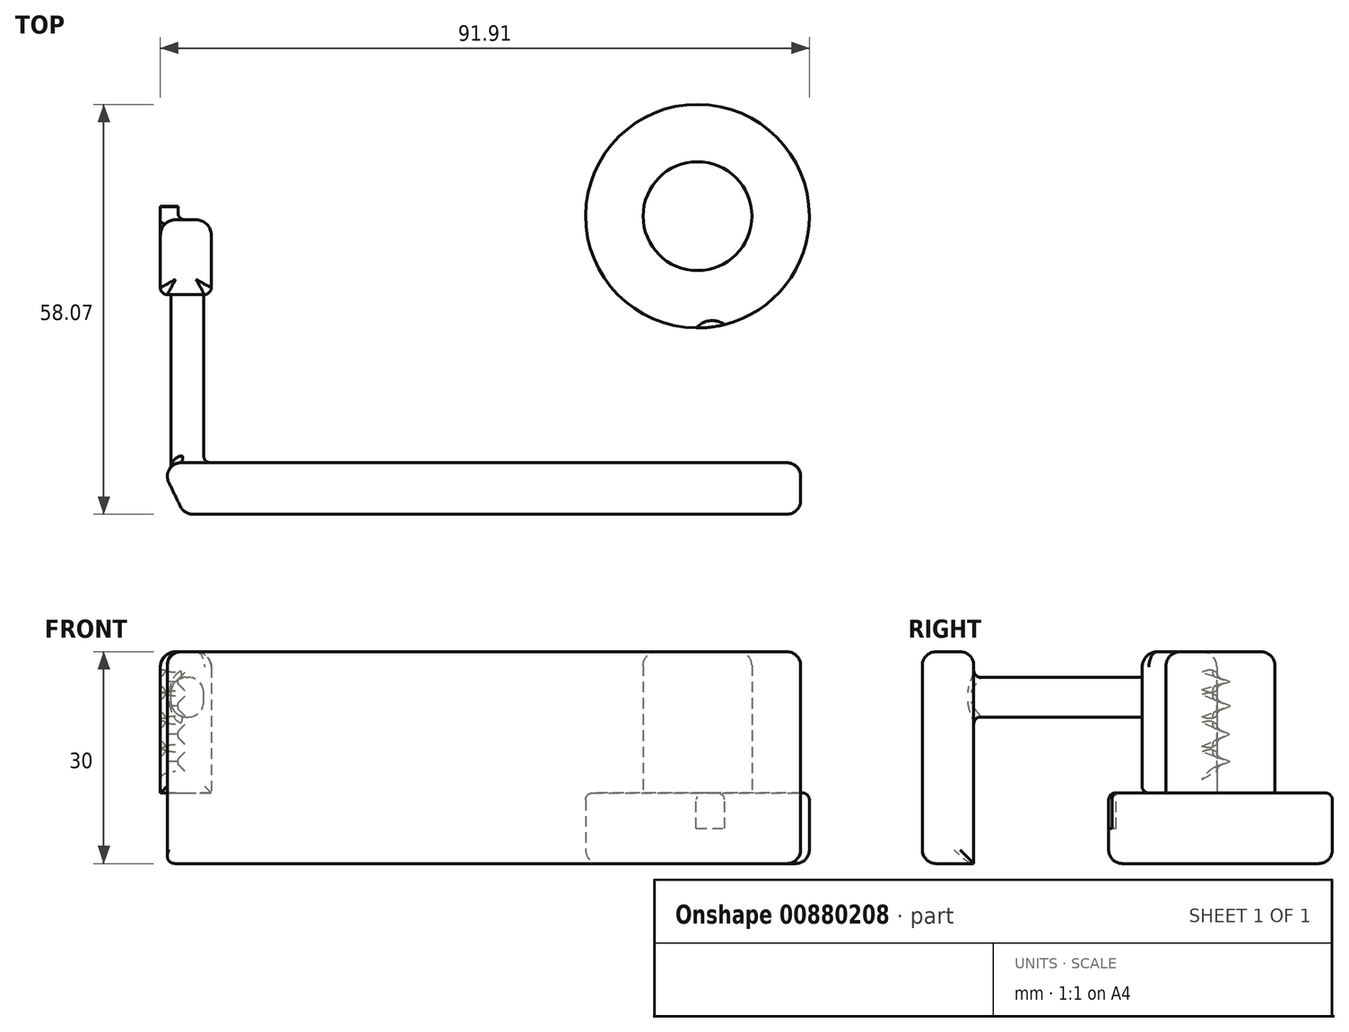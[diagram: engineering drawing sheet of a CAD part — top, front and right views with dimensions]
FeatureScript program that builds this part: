
annotation { "Feature Type Name" : "Feature", "Feature Type Description" : "" }
export const myFeature = defineFeature(function(context is Context, id is Id, definition is map)
    precondition{}
    {
        {
            var Q0;
            Q0=qCreatedBy(makeId("Top.planeOp"),FACE);
            var sketch = newSketch(context, id + "F0", { "sketchPlane" : qUnion([Q0])});
            skLineSegment(sketch, "E0", {"start": v(63.05, -17.14) * mm, "end": v(63.05, 11.68) * mm});
            skCircle(sketch, "E1", {"center": v(48.44, 17.8) * mm, "radius": 15.84 * mm});
            skFitSpline(sketch, "E2", {"points": [v(35.46, 26.9) * mm, v(16.93, 8.4) * mm, v(-6.27, 10.49) * mm, v(-19.03, 21.44) * mm, v(-36, 19.85) * mm, v(-24.25, -24.43) * mm], "startDerivative": vector(-84.65, -85.57) * mm, "endDerivative": vector(94.53, -192.44) * mm});
            skLineSegment(sketch, "E3", {"start": v(-27.75, -17.14) * mm, "end": v(63.05, -17.14) * mm});
            skLineSegment(sketch, "E4", {"start": v(-24.25, -24.43) * mm, "end": v(63.05, -24.43) * mm});
            skLineSegment(sketch, "E5", {"start": v(63.05, -24.43) * mm, "end": v(63.05, -17.14) * mm});
            skSolve(sketch);
        }
        {
            var Q0;
            {var subQ0=sQuery(id+"F0.wireOp",EDGE,"E1");var subQ1=makeQuery(id+"F0.imprint","INTERSECT",VERTEX,{"derivedFrom":[sQuery(id+"F0.wireOp",EDGE,"E0"),subQ0]});Q0=makeQuery(id+"F0.imprint","IMPRINT",FACE,{"disambiguationData":[TD([[makeQuery(id+"F0.imprint","IMPRINT",EDGE,{"disambiguationData":[TD([[subQ1,1.0]])],"derivedFrom":subQ0}),1.0]])]});}
            var Q1;
            {var subQ0=sQuery(id+"F0.wireOp",EDGE,"E0");Q1=makeQuery(id+"F0.imprint","IMPRINT",FACE,{"disambiguationData":[TD([[makeQuery(id+"F0.imprint","IMPRINT",EDGE,{"derivedFrom":subQ0}),1.0]])]});}
            extrude(context, id + "F1", {"entities" : qUnion([Q0, Q1]), "depth" : 10 * mm, "offsetDistance" : 25.4 * mm});
        }
        {
            var Q0;
            {var subQ2=sQuery(id+"F0.wireOp",EDGE,"E3");Q0=makeQuery(id+"F0.imprint","IMPRINT",FACE,{"disambiguationData":[TD([[makeQuery(id+"F0.imprint","IMPRINT",EDGE,{"derivedFrom":subQ2}),-1.0]])]});}
            extrude(context, id + "F2", {"entities" : qUnion([Q0]), "operationType" : NewBodyOperationType.ADD, "depth" : 30 * mm, "offsetDistance" : 25 * mm});
        }
        {
            var Q0;
            Q0=makeQuery(id+"F1.opExtrude","CAP_FACE",FACE,{"disambiguationData":[OSD([sQuery(id+"F0.wireOp",EDGE,"E0"),sQuery(id+"F0.wireOp",EDGE,"E1"),sQuery(id+"F0.wireOp",EDGE,"E2"),sQuery(id+"F0.wireOp",EDGE,"E3")])],"isStart":false});
            var sketch = newSketch(context, id + "F3", { "sketchPlane" : qUnion([Q0])});
            skCircle(sketch, "E6", {"center": v(48.44, 17.8) * mm, "radius": 7.7 * mm});
            skLineSegment(sketch, "E7.bottom", {"start": v(-27.63, 17.29) * mm, "end": v(-20.42, 17.29) * mm});
            skLineSegment(sketch, "E7.top", {"start": v(-27.63, 6.69) * mm, "end": v(-20.42, 6.69) * mm});
            skLineSegment(sketch, "E7.left", {"start": v(-27.63, 17.29) * mm, "end": v(-27.63, 6.69) * mm});
            skLineSegment(sketch, "E7.right", {"start": v(-20.42, 17.29) * mm, "end": v(-20.42, 6.69) * mm});
            skPoint(sketch, "E8", {"position": v(-8.96, 0) * mm});
            skPoint(sketch, "E9", {"position": v(20.74, 0) * mm});
            skPoint(sketch, "E10", {"position": v(50.52, 0) * mm});
            skSolve(sketch);
        }
        {
            var Q0;
            Q0=makeQuery(id+"F3.imprint","IMPRINT",FACE,{"disambiguationData":[TD([[makeQuery(id+"F3.imprint","IMPRINT",EDGE,{"derivedFrom":sQuery(id+"F3.wireOp",EDGE,"E6")}),1.0]])]});
            var Q1;
            Q1=makeQuery(id+"F3.imprint","IMPRINT",FACE,{"disambiguationData":[TD([[makeQuery(id+"F3.imprint","IMPRINT",EDGE,{"derivedFrom":sQuery(id+"F3.wireOp",EDGE,"E7.bottom")}),-1.0]])]});
            extrude(context, id + "F4", {"entities" : qUnion([Q0, Q1]), "operationType" : NewBodyOperationType.ADD, "depth" : 20 * mm, "offsetDistance" : 25 * mm});
        }
        {
            var Q0;
            Q0=makeQuery(id+"F4.opExtrude","SWEPT_FACE",FACE,{"disambiguationData":[OSD([sQuery(id+"F3.wireOp",EDGE,"E7.left")])]});
            var sketch = newSketch(context, id + "F5", { "sketchPlane" : qUnion([Q0])});
            skLineSegment(sketch, "E11", {"start": v(-17.29, 13.76) * mm, "end": v(-19.15, 14.47) * mm});
            skLineSegment(sketch, "E12", {"start": v(-19.15, 14.47) * mm, "end": v(-14.05, 16.16) * mm});
            skLineSegment(sketch, "E13", {"start": v(-14.05, 16.16) * mm, "end": v(-19.09, 18.3) * mm});
            skLineSegment(sketch, "E14", {"start": v(-19.09, 18.3) * mm, "end": v(-14.05, 20.42) * mm});
            skLineSegment(sketch, "E15", {"start": v(-14.05, 20.42) * mm, "end": v(-19.2, 22.3) * mm});
            skLineSegment(sketch, "E16", {"start": v(-19.2, 22.3) * mm, "end": v(-14.05, 24.37) * mm});
            skLineSegment(sketch, "E17.bottom", {"start": v(-17.29, 10) * mm, "end": v(-6.69, 10) * mm});
            skLineSegment(sketch, "E17.top", {"start": v(-17.29, 30) * mm, "end": v(-6.69, 30) * mm});
            skLineSegment(sketch, "E17.left", {"start": v(-17.29, 10) * mm, "end": v(-17.29, 30) * mm});
            skLineSegment(sketch, "E17.right", {"start": v(-6.69, 10) * mm, "end": v(-6.69, 30) * mm});
            skLineSegment(sketch, "E18", {"start": v(-14.05, 24.37) * mm, "end": v(-19.15, 25.75) * mm});
            skLineSegment(sketch, "E19", {"start": v(-19.15, 25.75) * mm, "end": v(-17.29, 26.37) * mm});
            skSolve(sketch);
        }
        {
            var Q0;
            Q0 = qSketchRegion(id + "F5", true);
            extrude(context, id + "F6", {"entities" : qUnion([Q0]), "operationType" : NewBodyOperationType.ADD, "oppositeDirection" : true, "depth" : 2.5 * mm, "offsetDistance" : 25 * mm});
        }
        {
            var Q0;
            Q0=makeQuery(id+"F4.opExtrude","SWEPT_FACE",FACE,{"disambiguationData":[OSD([sQuery(id+"F3.wireOp",EDGE,"E7.top")])]});
            var sketch = newSketch(context, id + "F7", { "sketchPlane" : qUnion([Q0])});
            skLineSegment(sketch, "E20.bottom", {"start": v(-26.13, 20.76) * mm, "end": v(-21.5, 20.76) * mm});
            skLineSegment(sketch, "E20.top", {"start": v(-26.13, 26.39) * mm, "end": v(-21.5, 26.39) * mm});
            skLineSegment(sketch, "E20.left", {"start": v(-26.13, 20.76) * mm, "end": v(-26.13, 26.39) * mm});
            skLineSegment(sketch, "E20.right", {"start": v(-21.5, 20.76) * mm, "end": v(-21.5, 26.39) * mm});
            skSolve(sketch);
        }
        {
            var Q0;
            Q0 = qSketchRegion(id + "F7", true);
            extrude(context, id + "F8", {"entities" : qUnion([Q0]), "operationType" : NewBodyOperationType.ADD, "depth" : 25 * mm, "offsetDistance" : 25 * mm});
        }
        {
            var Q0;
            Q0=sQuery(id+"F3.wireOp",VERTEX,"E8");
            var Q1;
            Q1=sQuery(id+"F3.wireOp",VERTEX,"E9");
            var Q2;
            Q2=sQuery(id+"F3.wireOp",VERTEX,"E10");
            var Q3;
            Q3=makeQuery(id+"F1.opExtrude","SWEPT_BODY",BODY,{"disambiguationData":[OSD([sQuery(id+"F0.wireOp",EDGE,"E0"),sQuery(id+"F0.wireOp",EDGE,"E1"),sQuery(id+"F0.wireOp",EDGE,"E2"),sQuery(id+"F0.wireOp",EDGE,"E3")])]});
            hole(context, id + "F9", {"style" : HoleStyle.C_BORE, "endStyle" : HoleEndStyle.THROUGH, "holeDiameter" : 4 * mm, "cBoreDiameter" : 6 * mm, "cBoreDepth" : 5 * mm, "majorDiameter" : 5 * mm, "isTappedThrough" : true, "tappedDepth" : 12 * mm, "tapClearance" : 3, "locations" : qUnion([Q0, Q1, Q2]), "scope" : qUnion([Q3])});
        }
        {
            var Q0;
            Q0=makeQuery(id+"F2.opExtrude","SWEPT_EDGE",EDGE,{"disambiguationData":[OSD([sQuery(id+"F0.wireOp",EDGE,"E2"),sQuery(id+"F0.wireOp",EDGE,"E4")])]});
            var Q1;
            Q1=makeQuery(id+"F2.opExtrude","CAP_EDGE",EDGE,{"disambiguationData":[OSD([sQuery(id+"F0.wireOp",EDGE,"E4")])],"isStart":false});
            var Q2;
            Q2=makeQuery(id+"F2.opExtrude","SWEPT_EDGE",EDGE,{"disambiguationData":[OSD([sQuery(id+"F0.wireOp",EDGE,"E4"),sQuery(id+"F0.wireOp",EDGE,"E5")])]});
            var Q3;
            Q3=makeQuery(id+"F2.opExtrude","CAP_EDGE",EDGE,{"disambiguationData":[OSD([sQuery(id+"F0.wireOp",EDGE,"E4")])],"isStart":true});
            var Q4;
            {var subQ0=sQuery(id+"F0.wireOp",EDGE,"E2");Q4=makeQuery(id+"F2.boolean.opBoolean","MERGE",EDGE,{"derivedFrom":[makeQuery(id+"F1.opExtrude","CAP_EDGE",EDGE,{"disambiguationData":[OSD([subQ0])],"isStart":true}),makeQuery(id+"F2.opExtrude","CAP_EDGE",EDGE,{"disambiguationData":[OSD([subQ0])],"isStart":true})]});}
            var Q5;
            Q5=makeQuery(id+"F1.opExtrude","CAP_EDGE",EDGE,{"disambiguationData":[OSD([sQuery(id+"F0.wireOp",EDGE,"E1")])],"isStart":true});
            var Q6;
            Q6=makeQuery(id+"F2.boolean.opBoolean","MERGE",EDGE,{"derivedFrom":[makeQuery(id+"F1.opExtrude","CAP_EDGE",EDGE,{"disambiguationData":[OSD([sQuery(id+"F0.wireOp",EDGE,"E0")])],"isStart":true}),makeQuery(id+"F2.opExtrude","CAP_EDGE",EDGE,{"disambiguationData":[OSD([sQuery(id+"F0.wireOp",EDGE,"E5")])],"isStart":true})]});
            var Q7;
            Q7=makeQuery(id+"F1.opExtrude","CAP_EDGE",EDGE,{"disambiguationData":[OSD([sQuery(id+"F0.wireOp",EDGE,"E2")])],"isStart":false});
            var Q8;
            Q8=makeQuery(id+"F2.opExtrude","SWEPT_EDGE",EDGE,{"disambiguationData":[OSD([sQuery(id+"F0.wireOp",EDGE,"E0"),sQuery(id+"F0.wireOp",EDGE,"E3"),sQuery(id+"F0.wireOp",EDGE,"E5")])]});
            var Q9;
            Q9=makeQuery(id+"F2.opExtrude","CAP_EDGE",EDGE,{"disambiguationData":[OSD([sQuery(id+"F0.wireOp",EDGE,"E5")])],"isStart":false});
            var Q10;
            Q10=makeQuery(id+"F2.opExtrude","CAP_EDGE",EDGE,{"disambiguationData":[OSD([sQuery(id+"F0.wireOp",EDGE,"E3")])],"isStart":false});
            var Q11;
            Q11=makeQuery(id+"F2.opExtrude","SWEPT_EDGE",EDGE,{"disambiguationData":[OSD([sQuery(id+"F0.wireOp",EDGE,"E2"),sQuery(id+"F0.wireOp",EDGE,"E3")])]});
            var Q12;
            Q12=makeQuery(id+"F2.opExtrude","CAP_EDGE",EDGE,{"disambiguationData":[OSD([sQuery(id+"F0.wireOp",EDGE,"E2")])],"isStart":false});
            var Q13;
            Q13=makeQuery(id+"F4.opExtrude","CAP_EDGE",EDGE,{"disambiguationData":[OSD([sQuery(id+"F3.wireOp",EDGE,"E6")])],"isStart":false});
            var Q14;
            Q14=makeQuery(id+"F1.opExtrude","CAP_EDGE",EDGE,{"disambiguationData":[OSD([sQuery(id+"F0.wireOp",EDGE,"E3")])],"isStart":false});
            fillet(context, id + "F10", {"entities" : qUnion([Q0, Q1, Q2, Q3, Q4, Q5, Q6, Q7, Q8, Q9, Q10, Q11, Q12, Q13, Q14]), "radius" : 1.93 * mm, "tangentPropagation" : true, "allowEdgeOverflow" : false});
        }
        {
            var Q0;
            Q0=makeQuery(id+"F1.opExtrude","CAP_EDGE",EDGE,{"disambiguationData":[OSD([sQuery(id+"F0.wireOp",EDGE,"E0")])],"isStart":false});
            var Q1;
            Q1=makeQuery(id+"F8.opExtrude","SWEPT_EDGE",EDGE,{"disambiguationData":[OSD([sQuery(id+"F7.wireOp",EDGE,"E20.top"),sQuery(id+"F7.wireOp",EDGE,"E20.left")])]});
            var Q2;
            Q2=makeQuery(id+"F8.opExtrude","SWEPT_EDGE",EDGE,{"disambiguationData":[OSD([sQuery(id+"F7.wireOp",EDGE,"E20.bottom"),sQuery(id+"F7.wireOp",EDGE,"E20.left")])]});
            var Q3;
            Q3=makeQuery(id+"F8.opExtrude","SWEPT_EDGE",EDGE,{"disambiguationData":[OSD([sQuery(id+"F7.wireOp",EDGE,"E20.top"),sQuery(id+"F7.wireOp",EDGE,"E20.right")])]});
            var Q4;
            Q4=makeQuery(id+"F8.opExtrude","SWEPT_EDGE",EDGE,{"disambiguationData":[OSD([sQuery(id+"F7.wireOp",EDGE,"E20.bottom"),sQuery(id+"F7.wireOp",EDGE,"E20.right")])]});
            var Q5;
            Q5=makeQuery(id+"F4.opExtrude","CAP_EDGE",EDGE,{"disambiguationData":[OSD([sQuery(id+"F3.wireOp",EDGE,"E7.top")])],"isStart":false});
            var Q6;
            Q6=makeQuery(id+"F4.opExtrude","CAP_EDGE",EDGE,{"disambiguationData":[OSD([sQuery(id+"F3.wireOp",EDGE,"E7.left")])],"isStart":false});
            var Q7;
            Q7=makeQuery(id+"F4.opExtrude","CAP_EDGE",EDGE,{"disambiguationData":[OSD([sQuery(id+"F3.wireOp",EDGE,"E7.right")])],"isStart":false});
            var Q8;
            Q8=makeQuery(id+"F4.opExtrude","CAP_EDGE",EDGE,{"disambiguationData":[OSD([sQuery(id+"F3.wireOp",EDGE,"E7.bottom")])],"isStart":false});
            var Q9;
            Q9=makeQuery(id+"F4.opExtrude","SWEPT_EDGE",EDGE,{"disambiguationData":[OSD([sQuery(id+"F3.wireOp",EDGE,"E7.bottom"),sQuery(id+"F3.wireOp",EDGE,"E7.right")])]});
            var Q10;
            {var subQ0=sQuery(id+"F5.wireOp",EDGE,"E14");var subQ2=sQuery(id+"F3.wireOp",EDGE,"E7.left");var subQ3=sQuery(id+"F3.wireOp",EDGE,"E7.bottom");Q10=makeQuery(id+"F6.boolean.opBoolean","SPLIT",EDGE,{"disambiguationData":[TD([makeQuery(id+"F6.opExtrude","SWEPT_FACE",FACE,{"disambiguationData":[OSD([subQ0])]})])],"derivedFrom":makeQuery(id+"F4.opExtrude","SWEPT_EDGE",EDGE,{"disambiguationData":[OSD([subQ3,subQ2])]})});}
            var Q11;
            {var subQ0=sQuery(id+"F5.wireOp",EDGE,"E16");var subQ2=sQuery(id+"F3.wireOp",EDGE,"E7.left");var subQ3=sQuery(id+"F3.wireOp",EDGE,"E7.bottom");Q11=makeQuery(id+"F6.boolean.opBoolean","SPLIT",EDGE,{"disambiguationData":[TD([makeQuery(id+"F6.opExtrude","SWEPT_FACE",FACE,{"disambiguationData":[OSD([subQ0])]})])],"derivedFrom":makeQuery(id+"F4.opExtrude","SWEPT_EDGE",EDGE,{"disambiguationData":[OSD([subQ3,subQ2])]})});}
            var Q12;
            {var subQ0=sQuery(id+"F3.wireOp",EDGE,"E7.left");var subQ1=sQuery(id+"F5.wireOp",EDGE,"E19");var subQ2=sQuery(id+"F3.wireOp",EDGE,"E7.bottom");Q12=makeQuery(id+"F6.boolean.opBoolean","SPLIT",EDGE,{"disambiguationData":[TD([makeQuery(id+"F6.opExtrude","SWEPT_FACE",FACE,{"disambiguationData":[OSD([subQ1])]})])],"derivedFrom":makeQuery(id+"F4.opExtrude","SWEPT_EDGE",EDGE,{"disambiguationData":[OSD([subQ2,subQ0])]})});}
            var Q13;
            {var subQ0=sQuery(id+"F5.wireOp",EDGE,"E11");var subQ1=sQuery(id+"F3.wireOp",EDGE,"E7.bottom");var subQ2=sQuery(id+"F3.wireOp",EDGE,"E7.left");Q13=makeQuery(id+"F6.boolean.opBoolean","SPLIT",EDGE,{"disambiguationData":[TD([makeQuery(id+"F6.opExtrude","SWEPT_FACE",FACE,{"disambiguationData":[OSD([subQ0])]})])],"derivedFrom":makeQuery(id+"F4.opExtrude","SWEPT_EDGE",EDGE,{"disambiguationData":[OSD([subQ1,subQ2])]})});}
            var Q14;
            {var subQ1=sQuery(id+"F5.wireOp",EDGE,"E12");var subQ2=sQuery(id+"F3.wireOp",EDGE,"E7.left");var subQ3=sQuery(id+"F3.wireOp",EDGE,"E7.bottom");Q14=makeQuery(id+"F6.boolean.opBoolean","SPLIT",EDGE,{"disambiguationData":[TD([makeQuery(id+"F6.opExtrude","SWEPT_FACE",FACE,{"disambiguationData":[OSD([subQ1])]})])],"derivedFrom":makeQuery(id+"F4.opExtrude","SWEPT_EDGE",EDGE,{"disambiguationData":[OSD([subQ3,subQ2])]})});}
            fillet(context, id + "F11", {"entities" : qUnion([Q0, Q1, Q2, Q3, Q4, Q5, Q6, Q7, Q8, Q9, Q10, Q11, Q12, Q13, Q14]), "radius" : 2.17 * mm, "tangentPropagation" : true, "allowEdgeOverflow" : false});
        }
        {
            var Q0;
            Q0=makeQuery(id+"F9.hole-2.boolean.opBoolean","COPY",EDGE,{"derivedFrom":makeQuery(id+"F9.hole-2.opRevolve","SWEPT_EDGE",EDGE,{"disambiguationData":[OSD([sQuery(id+"F9.hole-2.sketch.wireOp",EDGE,"cbore_start_line_2"),sQuery(id+"F9.hole-2.sketch.wireOp",EDGE,"cbore_start_line_3")])]})});
            var Q1;
            Q1=makeQuery(id+"F9.hole-1.boolean.opBoolean","COPY",EDGE,{"derivedFrom":makeQuery(id+"F9.hole-1.opRevolve","SWEPT_EDGE",EDGE,{"disambiguationData":[OSD([sQuery(id+"F9.hole-1.sketch.wireOp",EDGE,"cbore_start_line_2"),sQuery(id+"F9.hole-1.sketch.wireOp",EDGE,"cbore_start_line_3")])]})});
            var Q2;
            Q2=makeQuery(id+"F9.hole-0.boolean.opBoolean","COPY",EDGE,{"derivedFrom":makeQuery(id+"F9.hole-0.opRevolve","SWEPT_EDGE",EDGE,{"disambiguationData":[OSD([sQuery(id+"F9.hole-0.sketch.wireOp",EDGE,"cbore_start_line_2"),sQuery(id+"F9.hole-0.sketch.wireOp",EDGE,"cbore_start_line_3")])]})});
            var Q3;
            {var subQ0=sQuery(id+"F0.wireOp",EDGE,"E3");var subQ1=sQuery(id+"F0.wireOp",EDGE,"E2");Q3=makeQuery(id+"F11.opFillet","BLEND_EDGE",EDGE,{"blendedFrom":[makeQuery(id+"F8.opExtrude","SWEPT_EDGE",EDGE,{"disambiguationData":[OSD([sQuery(id+"F7.wireOp",EDGE,"E20.top"),sQuery(id+"F7.wireOp",EDGE,"E20.left")])]}),makeQuery(id+"F10.opFillet","BLEND_FACE",FACE,{"disambiguationData":[OSD([subQ1,subQ0]),TDD([makeQuery(id+"F2.opExtrude","SWEPT_EDGE",EDGE,{"disambiguationData":[OSD([subQ1,subQ0])]})])]})],"blendedInto":[makeQuery(id+"F10.opFillet","BLEND_FACE",FACE,{"disambiguationData":[OSD([subQ1,subQ0]),TDD([makeQuery(id+"F2.opExtrude","SWEPT_EDGE",EDGE,{"disambiguationData":[OSD([subQ1,subQ0])]})])]})]});}
            var Q4;
            Q4=makeQuery(id+"F4.opExtrude","CAP_EDGE",EDGE,{"disambiguationData":[OSD([sQuery(id+"F3.wireOp",EDGE,"E7.top")])],"isStart":true});
            var Q5;
            Q5=makeQuery(id+"F4.opExtrude","SWEPT_EDGE",EDGE,{"disambiguationData":[OSD([sQuery(id+"F3.wireOp",EDGE,"E7.top"),sQuery(id+"F3.wireOp",EDGE,"E7.left")])]});
            var Q6;
            Q6=makeQuery(id+"F4.opExtrude","SWEPT_EDGE",EDGE,{"disambiguationData":[OSD([sQuery(id+"F3.wireOp",EDGE,"E7.top"),sQuery(id+"F3.wireOp",EDGE,"E7.right")])]});
            var Q7;
            {var subQ0=sQuery(id+"F5.wireOp",EDGE,"E12");var subQ1=makeQuery(id+"F6.opExtrude","SWEPT_FACE",FACE,{"disambiguationData":[OSD([subQ0])]});var subQ3=sQuery(id+"F3.wireOp",EDGE,"E7.left");var subQ4=sQuery(id+"F3.wireOp",EDGE,"E7.bottom");Q7=makeQuery(id+"F11.opFillet","BLEND_EDGE",EDGE,{"blendedFrom":[makeQuery(id+"F6.boolean.opBoolean","SPLIT",EDGE,{"disambiguationData":[TD([subQ1])],"derivedFrom":makeQuery(id+"F4.opExtrude","SWEPT_EDGE",EDGE,{"disambiguationData":[OSD([subQ4,subQ3])]})}),subQ1],"blendedInto":[subQ1]});}
            var Q8;
            {var subQ0=sQuery(id+"F5.wireOp",EDGE,"E14");var subQ1=makeQuery(id+"F6.opExtrude","SWEPT_FACE",FACE,{"disambiguationData":[OSD([subQ0])]});var subQ3=sQuery(id+"F3.wireOp",EDGE,"E7.left");var subQ4=sQuery(id+"F3.wireOp",EDGE,"E7.bottom");Q8=makeQuery(id+"F11.opFillet","BLEND_EDGE",EDGE,{"blendedFrom":[makeQuery(id+"F6.boolean.opBoolean","SPLIT",EDGE,{"disambiguationData":[TD([subQ1])],"derivedFrom":makeQuery(id+"F4.opExtrude","SWEPT_EDGE",EDGE,{"disambiguationData":[OSD([subQ4,subQ3])]})}),subQ1],"blendedInto":[subQ1]});}
            var Q9;
            {var subQ0=sQuery(id+"F5.wireOp",EDGE,"E16");var subQ1=makeQuery(id+"F6.opExtrude","SWEPT_FACE",FACE,{"disambiguationData":[OSD([subQ0])]});var subQ3=sQuery(id+"F3.wireOp",EDGE,"E7.left");var subQ4=sQuery(id+"F3.wireOp",EDGE,"E7.bottom");Q9=makeQuery(id+"F11.opFillet","BLEND_EDGE",EDGE,{"blendedFrom":[makeQuery(id+"F6.boolean.opBoolean","SPLIT",EDGE,{"disambiguationData":[TD([subQ1])],"derivedFrom":makeQuery(id+"F4.opExtrude","SWEPT_EDGE",EDGE,{"disambiguationData":[OSD([subQ4,subQ3])]})}),subQ1],"blendedInto":[subQ1]});}
            var Q10;
            {var subQ0=sQuery(id+"F5.wireOp",EDGE,"E19");var subQ1=makeQuery(id+"F6.opExtrude","SWEPT_FACE",FACE,{"disambiguationData":[OSD([subQ0])]});var subQ2=sQuery(id+"F3.wireOp",EDGE,"E7.left");var subQ3=sQuery(id+"F3.wireOp",EDGE,"E7.bottom");Q10=makeQuery(id+"F11.opFillet","BLEND_EDGE",EDGE,{"blendedFrom":[makeQuery(id+"F6.boolean.opBoolean","SPLIT",EDGE,{"disambiguationData":[TD([subQ1])],"derivedFrom":makeQuery(id+"F4.opExtrude","SWEPT_EDGE",EDGE,{"disambiguationData":[OSD([subQ3,subQ2])]})}),subQ1],"blendedInto":[subQ1]});}
            var Q11;
            {var subQ0=sQuery(id+"F5.wireOp",EDGE,"E18");var subQ1=makeQuery(id+"F6.opExtrude","SWEPT_FACE",FACE,{"disambiguationData":[OSD([subQ0])]});var subQ2=sQuery(id+"F5.wireOp",EDGE,"E16");var subQ3=sQuery(id+"F3.wireOp",EDGE,"E7.left");var subQ4=sQuery(id+"F3.wireOp",EDGE,"E7.bottom");Q11=makeQuery(id+"F11.opFillet","BLEND_EDGE",EDGE,{"blendedFrom":[makeQuery(id+"F6.boolean.opBoolean","SPLIT",EDGE,{"disambiguationData":[TD([makeQuery(id+"F6.opExtrude","SWEPT_FACE",FACE,{"disambiguationData":[OSD([subQ2])]})])],"derivedFrom":makeQuery(id+"F4.opExtrude","SWEPT_EDGE",EDGE,{"disambiguationData":[OSD([subQ4,subQ3])]})}),subQ1],"blendedInto":[subQ1]});}
            var Q12;
            {var subQ0=sQuery(id+"F5.wireOp",EDGE,"E15");var subQ1=makeQuery(id+"F6.opExtrude","SWEPT_FACE",FACE,{"disambiguationData":[OSD([subQ0])]});var subQ2=sQuery(id+"F5.wireOp",EDGE,"E14");var subQ3=sQuery(id+"F3.wireOp",EDGE,"E7.left");var subQ4=sQuery(id+"F3.wireOp",EDGE,"E7.bottom");Q12=makeQuery(id+"F11.opFillet","BLEND_EDGE",EDGE,{"blendedFrom":[makeQuery(id+"F6.boolean.opBoolean","SPLIT",EDGE,{"disambiguationData":[TD([makeQuery(id+"F6.opExtrude","SWEPT_FACE",FACE,{"disambiguationData":[OSD([subQ2])]})])],"derivedFrom":makeQuery(id+"F4.opExtrude","SWEPT_EDGE",EDGE,{"disambiguationData":[OSD([subQ4,subQ3])]})}),subQ1],"blendedInto":[subQ1]});}
            var Q13;
            {var subQ0=sQuery(id+"F5.wireOp",EDGE,"E13");var subQ1=makeQuery(id+"F6.opExtrude","SWEPT_FACE",FACE,{"disambiguationData":[OSD([subQ0])]});var subQ2=sQuery(id+"F5.wireOp",EDGE,"E12");var subQ3=sQuery(id+"F3.wireOp",EDGE,"E7.left");var subQ4=sQuery(id+"F3.wireOp",EDGE,"E7.bottom");Q13=makeQuery(id+"F11.opFillet","BLEND_EDGE",EDGE,{"blendedFrom":[makeQuery(id+"F6.boolean.opBoolean","SPLIT",EDGE,{"disambiguationData":[TD([makeQuery(id+"F6.opExtrude","SWEPT_FACE",FACE,{"disambiguationData":[OSD([subQ2])]})])],"derivedFrom":makeQuery(id+"F4.opExtrude","SWEPT_EDGE",EDGE,{"disambiguationData":[OSD([subQ4,subQ3])]})}),subQ1],"blendedInto":[subQ1]});}
            var Q14;
            {var subQ0=sQuery(id+"F5.wireOp",EDGE,"E11");var subQ1=makeQuery(id+"F6.opExtrude","SWEPT_FACE",FACE,{"disambiguationData":[OSD([subQ0])]});var subQ2=sQuery(id+"F3.wireOp",EDGE,"E7.bottom");var subQ3=sQuery(id+"F3.wireOp",EDGE,"E7.left");Q14=makeQuery(id+"F11.opFillet","BLEND_EDGE",EDGE,{"blendedFrom":[makeQuery(id+"F6.boolean.opBoolean","SPLIT",EDGE,{"disambiguationData":[TD([subQ1])],"derivedFrom":makeQuery(id+"F4.opExtrude","SWEPT_EDGE",EDGE,{"disambiguationData":[OSD([subQ2,subQ3])]})}),subQ1],"blendedInto":[subQ1]});}
            var Q15;
            Q15=makeQuery(id+"F6.boolean.opBoolean","INTERSECT",EDGE,{"disambiguationData":[OD(1.0)],"derivedFrom":[makeQuery(id+"F4.opExtrude","SWEPT_FACE",FACE,{"disambiguationData":[OSD([sQuery(id+"F3.wireOp",EDGE,"E7.bottom")])]}),makeQuery(id+"F6.opExtrude","CAP_FACE",FACE,{"disambiguationData":[OSD([sQuery(id+"F5.wireOp",EDGE,"E11"),sQuery(id+"F5.wireOp",EDGE,"E12"),sQuery(id+"F5.wireOp",EDGE,"E13"),sQuery(id+"F5.wireOp",EDGE,"E14"),sQuery(id+"F5.wireOp",EDGE,"E15"),sQuery(id+"F5.wireOp",EDGE,"E16"),sQuery(id+"F5.wireOp",EDGE,"E17.bottom"),sQuery(id+"F5.wireOp",EDGE,"E17.top"),sQuery(id+"F5.wireOp",EDGE,"E17.left"),sQuery(id+"F5.wireOp",EDGE,"E17.right"),sQuery(id+"F5.wireOp",EDGE,"E18"),sQuery(id+"F5.wireOp",EDGE,"E19")])],"isStart":false})]});
            var Q16;
            Q16=makeQuery(id+"F6.boolean.opBoolean","INTERSECT",EDGE,{"disambiguationData":[OD(3.0)],"derivedFrom":[makeQuery(id+"F4.opExtrude","SWEPT_FACE",FACE,{"disambiguationData":[OSD([sQuery(id+"F3.wireOp",EDGE,"E7.bottom")])]}),makeQuery(id+"F6.opExtrude","CAP_FACE",FACE,{"disambiguationData":[OSD([sQuery(id+"F5.wireOp",EDGE,"E11"),sQuery(id+"F5.wireOp",EDGE,"E12"),sQuery(id+"F5.wireOp",EDGE,"E13"),sQuery(id+"F5.wireOp",EDGE,"E14"),sQuery(id+"F5.wireOp",EDGE,"E15"),sQuery(id+"F5.wireOp",EDGE,"E16"),sQuery(id+"F5.wireOp",EDGE,"E17.bottom"),sQuery(id+"F5.wireOp",EDGE,"E17.top"),sQuery(id+"F5.wireOp",EDGE,"E17.left"),sQuery(id+"F5.wireOp",EDGE,"E17.right"),sQuery(id+"F5.wireOp",EDGE,"E18"),sQuery(id+"F5.wireOp",EDGE,"E19")])],"isStart":false})]});
            var Q17;
            Q17=makeQuery(id+"F6.boolean.opBoolean","INTERSECT",EDGE,{"disambiguationData":[OD(2.0)],"derivedFrom":[makeQuery(id+"F4.opExtrude","SWEPT_FACE",FACE,{"disambiguationData":[OSD([sQuery(id+"F3.wireOp",EDGE,"E7.bottom")])]}),makeQuery(id+"F6.opExtrude","CAP_FACE",FACE,{"disambiguationData":[OSD([sQuery(id+"F5.wireOp",EDGE,"E11"),sQuery(id+"F5.wireOp",EDGE,"E12"),sQuery(id+"F5.wireOp",EDGE,"E13"),sQuery(id+"F5.wireOp",EDGE,"E14"),sQuery(id+"F5.wireOp",EDGE,"E15"),sQuery(id+"F5.wireOp",EDGE,"E16"),sQuery(id+"F5.wireOp",EDGE,"E17.bottom"),sQuery(id+"F5.wireOp",EDGE,"E17.top"),sQuery(id+"F5.wireOp",EDGE,"E17.left"),sQuery(id+"F5.wireOp",EDGE,"E17.right"),sQuery(id+"F5.wireOp",EDGE,"E18"),sQuery(id+"F5.wireOp",EDGE,"E19")])],"isStart":false})]});
            var Q18;
            Q18=makeQuery(id+"F6.boolean.opBoolean","INTERSECT",EDGE,{"disambiguationData":[OD(0.0)],"derivedFrom":[makeQuery(id+"F4.opExtrude","SWEPT_FACE",FACE,{"disambiguationData":[OSD([sQuery(id+"F3.wireOp",EDGE,"E7.bottom")])]}),makeQuery(id+"F6.opExtrude","CAP_FACE",FACE,{"disambiguationData":[OSD([sQuery(id+"F5.wireOp",EDGE,"E11"),sQuery(id+"F5.wireOp",EDGE,"E12"),sQuery(id+"F5.wireOp",EDGE,"E13"),sQuery(id+"F5.wireOp",EDGE,"E14"),sQuery(id+"F5.wireOp",EDGE,"E15"),sQuery(id+"F5.wireOp",EDGE,"E16"),sQuery(id+"F5.wireOp",EDGE,"E17.bottom"),sQuery(id+"F5.wireOp",EDGE,"E17.top"),sQuery(id+"F5.wireOp",EDGE,"E17.left"),sQuery(id+"F5.wireOp",EDGE,"E17.right"),sQuery(id+"F5.wireOp",EDGE,"E18"),sQuery(id+"F5.wireOp",EDGE,"E19")])],"isStart":false})]});
            var Q19;
            Q19=makeQuery(id+"F4.opExtrude","CAP_EDGE",EDGE,{"disambiguationData":[OSD([sQuery(id+"F3.wireOp",EDGE,"E6")])],"isStart":true});
            var Q20;
            Q20=makeQuery(id+"F1.opExtrude","CAP_EDGE",EDGE,{"disambiguationData":[OSD([sQuery(id+"F0.wireOp",EDGE,"E1")])],"isStart":false});
            var Q21;
            {var subQ0=sQuery(id+"F0.wireOp",EDGE,"E3");var subQ1=sQuery(id+"F0.wireOp",EDGE,"E2");Q21=makeQuery(id+"F9.hole-2.boolean.opBoolean","INTERSECT",EDGE,{"derivedFrom":[makeQuery(id+"F2.boolean.opBoolean","MERGE",FACE,{"derivedFrom":[makeQuery(id+"F1.opExtrude","CAP_FACE",FACE,{"disambiguationData":[OSD([sQuery(id+"F0.wireOp",EDGE,"E0"),sQuery(id+"F0.wireOp",EDGE,"E1"),subQ1,subQ0])],"isStart":true}),makeQuery(id+"F2.opExtrude","CAP_FACE",FACE,{"disambiguationData":[OSD([subQ1,subQ0,sQuery(id+"F0.wireOp",EDGE,"E4"),sQuery(id+"F0.wireOp",EDGE,"E5")])],"isStart":true})]}),makeQuery(id+"F9.hole-2.opRevolve","SWEPT_FACE",FACE,{"disambiguationData":[OSD([sQuery(id+"F9.hole-2.sketch.wireOp",EDGE,"core_line_2")])]})]});}
            var Q22;
            {var subQ0=sQuery(id+"F0.wireOp",EDGE,"E3");var subQ1=sQuery(id+"F0.wireOp",EDGE,"E2");Q22=makeQuery(id+"F9.hole-1.boolean.opBoolean","INTERSECT",EDGE,{"derivedFrom":[makeQuery(id+"F2.boolean.opBoolean","MERGE",FACE,{"derivedFrom":[makeQuery(id+"F1.opExtrude","CAP_FACE",FACE,{"disambiguationData":[OSD([sQuery(id+"F0.wireOp",EDGE,"E0"),sQuery(id+"F0.wireOp",EDGE,"E1"),subQ1,subQ0])],"isStart":true}),makeQuery(id+"F2.opExtrude","CAP_FACE",FACE,{"disambiguationData":[OSD([subQ1,subQ0,sQuery(id+"F0.wireOp",EDGE,"E4"),sQuery(id+"F0.wireOp",EDGE,"E5")])],"isStart":true})]}),makeQuery(id+"F9.hole-1.opRevolve","SWEPT_FACE",FACE,{"disambiguationData":[OSD([sQuery(id+"F9.hole-1.sketch.wireOp",EDGE,"core_line_2")])]})]});}
            var Q23;
            {var subQ0=sQuery(id+"F0.wireOp",EDGE,"E3");var subQ1=sQuery(id+"F0.wireOp",EDGE,"E2");Q23=makeQuery(id+"F9.hole-0.boolean.opBoolean","INTERSECT",EDGE,{"derivedFrom":[makeQuery(id+"F2.boolean.opBoolean","MERGE",FACE,{"derivedFrom":[makeQuery(id+"F1.opExtrude","CAP_FACE",FACE,{"disambiguationData":[OSD([sQuery(id+"F0.wireOp",EDGE,"E0"),sQuery(id+"F0.wireOp",EDGE,"E1"),subQ1,subQ0])],"isStart":true}),makeQuery(id+"F2.opExtrude","CAP_FACE",FACE,{"disambiguationData":[OSD([subQ1,subQ0,sQuery(id+"F0.wireOp",EDGE,"E4"),sQuery(id+"F0.wireOp",EDGE,"E5")])],"isStart":true})]}),makeQuery(id+"F9.hole-0.opRevolve","SWEPT_FACE",FACE,{"disambiguationData":[OSD([sQuery(id+"F9.hole-0.sketch.wireOp",EDGE,"core_line_2")])]})]});}
            fillet(context, id + "F12", {"entities" : qUnion([Q0, Q1, Q2, Q3, Q4, Q5, Q6, Q7, Q8, Q9, Q10, Q11, Q12, Q13, Q14, Q15, Q16, Q17, Q18, Q19, Q20, Q21, Q22, Q23]), "radius" : 0.97 * mm, "tangentPropagation" : true, "allowEdgeOverflow" : false});
        }
    });
